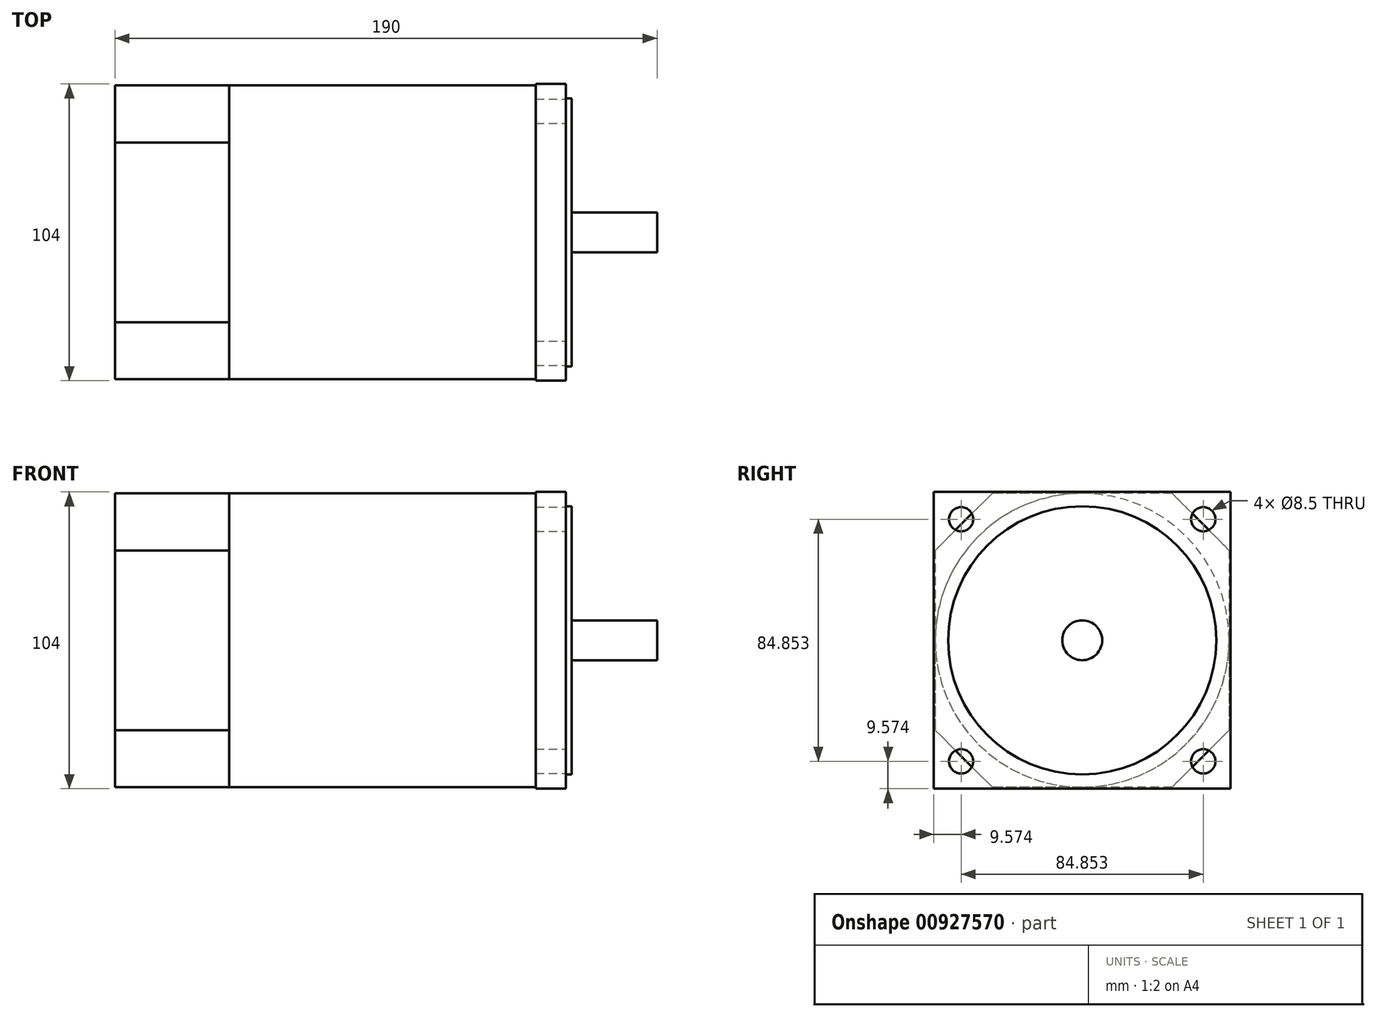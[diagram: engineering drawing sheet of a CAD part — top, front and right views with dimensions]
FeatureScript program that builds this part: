
annotation { "Feature Type Name" : "Feature", "Feature Type Description" : "" }
export const myFeature = defineFeature(function(context is Context, id is Id, definition is map)
    precondition{}
    {
        {
            var Q0;
            Q0=qCreatedBy(makeId("Right.planeOp"),FACE);
            var sketch = newSketch(context, id + "F0", { "sketchPlane" : qUnion([Q0])});
            skLineSegment(sketch, "E0.bottom", {"start": v(0, 0) * mm, "end": v(104, 0) * mm});
            skLineSegment(sketch, "E0.top", {"start": v(0, 104) * mm, "end": v(104, 104) * mm});
            skLineSegment(sketch, "E0.left", {"start": v(0, 0) * mm, "end": v(0, 104) * mm});
            skLineSegment(sketch, "E0.right", {"start": v(104, 0) * mm, "end": v(104, 104) * mm});
            skSolve(sketch);
        }
        {
            var Q0;
            Q0 = qSketchRegion(id + "F0", true);
            extrude(context, id + "F1", {"entities" : qUnion([Q0]), "oppositeDirection" : true, "depth" : 160 * mm, "offsetDistance" : 25 * mm});
        }
        {
            var Q0;
            Q0=qCreatedBy(makeId("Front.planeOp"),FACE);
            cPlane(context, id + "F2", {"entities" : qUnion([Q0]), "cplaneType" : CPlaneType.OFFSET, "offset" : (104 / 2) * mm, "oppositeDirection" : true, "width" : 150 * mm, "height" : 150 * mm});
        }
        {
            var Q0;
            Q0=qCreatedBy(id+"F2.planeOp",FACE);
            var sketch = newSketch(context, id + "F3", { "sketchPlane" : qUnion([Q0])});
            skLineSegment(sketch, "E1", {"start": v(-12.58, 109.9) * mm, "end": v(-12.58, -30.97) * mm, "construction": true});
            skLineSegment(sketch, "E2", {"start": v(-120, 120.54) * mm, "end": v(-120, -29.32) * mm, "construction": true});
            skLineSegment(sketch, "E3.bottom", {"start": v(-120, 143.5) * mm, "end": v(-12.58, 143.5) * mm});
            skLineSegment(sketch, "E3.top", {"start": v(-120, 103.5) * mm, "end": v(-12.58, 103.5) * mm});
            skLineSegment(sketch, "E3.left", {"start": v(-120, 143.5) * mm, "end": v(-120, 103.5) * mm});
            skLineSegment(sketch, "E3.right", {"start": v(-12.58, 143.5) * mm, "end": v(-12.58, 103.5) * mm});
            skLineSegment(sketch, "E4", {"start": v(-197.34, 52) * mm, "end": v(58.78, 52) * mm, "construction": true});
            skSolve(sketch);
        }
        {
            var Q0;
            Q0=makeQuery(id+"F3.imprint","IMPRINT",FACE,{"disambiguationData":[TD([[makeQuery(id+"F3.imprint","IMPRINT",EDGE,{"derivedFrom":sQuery(id+"F3.wireOp",EDGE,"E3.bottom")}),-1.0]])]});
            var Q1;
            Q1=sQuery(id+"F3.wireOp",EDGE,"E4");
            revolve(context, id + "F4", {"operationType" : NewBodyOperationType.REMOVE, "surfaceOperationType" : NewSurfaceOperationType.NEW, "entities" : qUnion([Q0]), "axis" : qUnion([Q1]), "revolveType" : RevolveType.FULL, "oppositeDirection" : true});
        }
        {
            var Q0;
            Q0=makeQuery(id+"F1.opExtrude","CAP_FACE",FACE,{"disambiguationData":[OSD([sQuery(id+"F0.wireOp",EDGE,"E0.bottom"),sQuery(id+"F0.wireOp",EDGE,"E0.top"),sQuery(id+"F0.wireOp",EDGE,"E0.left"),sQuery(id+"F0.wireOp",EDGE,"E0.right")])],"isStart":false});
            var sketch = newSketch(context, id + "F5", { "sketchPlane" : qUnion([Q0])});
            skLineSegment(sketch, "E5", {"start": v(-52, 107.46) * mm, "end": v(-52, -18.14) * mm, "construction": true});
            skLineSegment(sketch, "E6", {"start": v(-115.46, 52) * mm, "end": v(43.24, 52) * mm, "construction": true});
            skLineSegment(sketch, "E7.bottom", {"start": v(-103.5, 103.5) * mm, "end": v(-0.5, 103.5) * mm});
            skLineSegment(sketch, "E7.top", {"start": v(-103.5, 0.5) * mm, "end": v(-0.5, 0.5) * mm});
            skLineSegment(sketch, "E7.left", {"start": v(-103.5, 103.5) * mm, "end": v(-103.5, 0.5) * mm});
            skLineSegment(sketch, "E7.right", {"start": v(-0.5, 103.5) * mm, "end": v(-0.5, 0.5) * mm});
            skSolve(sketch);
        }
        {
            var Q0;
            Q0=makeQuery(id+"F5.imprint","IMPRINT",FACE,{"disambiguationData":[TD([[makeQuery(id+"F5.imprint","IMPRINT",EDGE,{"derivedFrom":sQuery(id+"F5.wireOp",EDGE,"E7.bottom")}),1.0]])]});
            extrude(context, id + "F6", {"entities" : qUnion([Q0]), "operationType" : NewBodyOperationType.REMOVE, "oppositeDirection" : true, "depth" : 40 * mm, "offsetDistance" : 25 * mm});
        }
        {
            var Q0;
            Q0=makeQuery(id+"F6.boolean.opBoolean","COPY",EDGE,{"derivedFrom":makeQuery(id+"F6.opExtrude","SWEPT_EDGE",EDGE,{"disambiguationData":[OSD([sQuery(id+"F5.wireOp",EDGE,"E7.bottom"),sQuery(id+"F5.wireOp",EDGE,"E7.right")])]})});
            var Q1;
            Q1=makeQuery(id+"F6.boolean.opBoolean","COPY",EDGE,{"derivedFrom":makeQuery(id+"F6.opExtrude","SWEPT_EDGE",EDGE,{"disambiguationData":[OSD([sQuery(id+"F5.wireOp",EDGE,"E7.bottom"),sQuery(id+"F5.wireOp",EDGE,"E7.left")])]})});
            var Q2;
            Q2=makeQuery(id+"F6.boolean.opBoolean","COPY",EDGE,{"derivedFrom":makeQuery(id+"F6.opExtrude","SWEPT_EDGE",EDGE,{"disambiguationData":[OSD([sQuery(id+"F5.wireOp",EDGE,"E7.top"),sQuery(id+"F5.wireOp",EDGE,"E7.left")])]})});
            var Q3;
            Q3=makeQuery(id+"F6.boolean.opBoolean","COPY",EDGE,{"derivedFrom":makeQuery(id+"F6.opExtrude","SWEPT_EDGE",EDGE,{"disambiguationData":[OSD([sQuery(id+"F5.wireOp",EDGE,"E7.top"),sQuery(id+"F5.wireOp",EDGE,"E7.right")])]})});
            chamfer(context, id + "F7", {"entities" : qUnion([Q0, Q1, Q2, Q3]), "width" : 20 * mm, "tangentPropagation" : true});
        }
        {
            var Q0;
            Q0=makeQuery(id+"F1.opExtrude","CAP_FACE",FACE,{"disambiguationData":[OSD([sQuery(id+"F0.wireOp",EDGE,"E0.bottom"),sQuery(id+"F0.wireOp",EDGE,"E0.top"),sQuery(id+"F0.wireOp",EDGE,"E0.left"),sQuery(id+"F0.wireOp",EDGE,"E0.right")])],"isStart":true});
            var sketch = newSketch(context, id + "F8", { "sketchPlane" : qUnion([Q0])});
            skLineSegment(sketch, "E8", {"start": v(52, 114.55) * mm, "end": v(52, -22.53) * mm, "construction": true});
            skPoint(sketch, "E8.startSnap0", {"position": v(52, 104) * mm});
            skLineSegment(sketch, "E9", {"start": v(-26.18, 52) * mm, "end": v(147.59, 52) * mm, "construction": true});
            skPoint(sketch, "E9.startSnap0", {"position": v(0, 52) * mm});
            skCircle(sketch, "E10", {"center": v(94.43, 94.43) * mm, "radius": 4.25 * mm});
            skPoint(sketch, "E11", {"position": v(52, 52) * mm});
            skLineSegment(sketch, "E12", {"start": v(0, 104) * mm, "end": v(104, 0) * mm, "construction": true});
            skLineSegment(sketch, "E13", {"start": v(0, 0) * mm, "end": v(104, 104) * mm, "construction": true});
            skCircle(sketch, "E14.MirrorC", {"center": v(94.43, 9.57) * mm, "radius": 4.25 * mm});
            skCircle(sketch, "E15.MirrorC", {"center": v(9.57, 94.43) * mm, "radius": 4.25 * mm});
            skCircle(sketch, "E16.MirrorC", {"center": v(9.57, 9.57) * mm, "radius": 4.25 * mm});
            skSolve(sketch);
        }
        {
            var Q0;
            Q0 = qSketchRegion(id + "F8", true);
            extrude(context, id + "F9", {"entities" : qUnion([Q0]), "operationType" : NewBodyOperationType.REMOVE, "oppositeDirection" : true, "depth" : 25 * mm, "offsetDistance" : 25 * mm});
        }
        {
            var Q0;
            Q0=makeQuery(id+"F1.opExtrude","CAP_FACE",FACE,{"disambiguationData":[OSD([sQuery(id+"F0.wireOp",EDGE,"E0.bottom"),sQuery(id+"F0.wireOp",EDGE,"E0.top"),sQuery(id+"F0.wireOp",EDGE,"E0.left"),sQuery(id+"F0.wireOp",EDGE,"E0.right")])],"isStart":true});
            var sketch = newSketch(context, id + "F10", { "sketchPlane" : qUnion([Q0])});
            skLineSegment(sketch, "E17", {"start": v(52, 115.05) * mm, "end": v(52, -18.98) * mm, "construction": true});
            skLineSegment(sketch, "E18", {"start": v(-11.66, 52) * mm, "end": v(147.16, 52) * mm, "construction": true});
            skCircle(sketch, "E19", {"center": v(52, 52) * mm, "radius": 7 * mm});
            skSolve(sketch);
        }
        {
            var Q0;
            Q0 = qSketchRegion(id + "F10", true);
            extrude(context, id + "F11", {"entities" : qUnion([Q0]), "operationType" : NewBodyOperationType.ADD, "depth" : 30 * mm, "offsetDistance" : 25 * mm});
        }
        {
            var Q0;
            Q0=makeQuery(id+"F1.opExtrude","CAP_FACE",FACE,{"disambiguationData":[OSD([sQuery(id+"F0.wireOp",EDGE,"E0.bottom"),sQuery(id+"F0.wireOp",EDGE,"E0.top"),sQuery(id+"F0.wireOp",EDGE,"E0.left"),sQuery(id+"F0.wireOp",EDGE,"E0.right")])],"isStart":true});
            var sketch = newSketch(context, id + "F12", { "sketchPlane" : qUnion([Q0])});
            skLineSegment(sketch, "E20", {"start": v(-17.03, 52) * mm, "end": v(125.3, 52) * mm, "construction": true});
            skPoint(sketch, "E20.startSnap0", {"position": v(0, 52) * mm});
            skLineSegment(sketch, "E21", {"start": v(52, 109.28) * mm, "end": v(52, -12.42) * mm, "construction": true});
            skPoint(sketch, "E21.startSnap0", {"position": v(52, 104) * mm});
            skPoint(sketch, "E22", {"position": v(52, 52) * mm});
            skCircle(sketch, "E23", {"center": v(52, 52) * mm, "radius": 47 * mm});
            skSolve(sketch);
        }
        {
            var Q0;
            Q0=makeQuery(id+"F12.imprint","IMPRINT",FACE,{"disambiguationData":[TD([[makeQuery(id+"F12.imprint","IMPRINT",EDGE,{"derivedFrom":sQuery(id+"F12.wireOp",EDGE,"E23")}),-1.0]])]});
            extrude(context, id + "F13", {"entities" : qUnion([Q0]), "operationType" : NewBodyOperationType.REMOVE, "oppositeDirection" : true, "depth" : 2 * mm, "offsetDistance" : 25 * mm});
        }
    });
